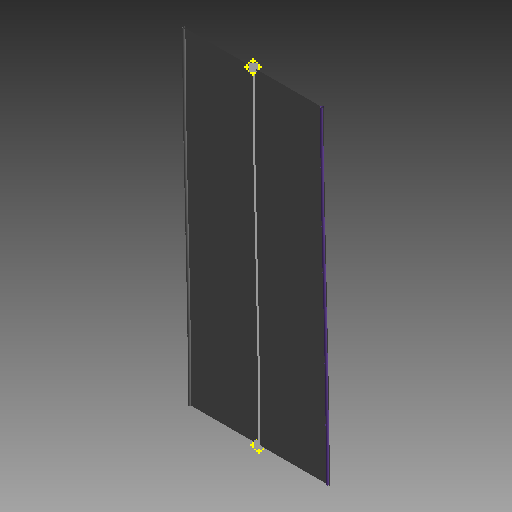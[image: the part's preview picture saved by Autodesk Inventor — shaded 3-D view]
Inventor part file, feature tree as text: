
AUTODESK INVENTOR PART (.ipt)
format: ipt  version: 2019 (Build 230136000, 136)  size: 113,664 bytes
history: native  units: mm (DEFAULTED — no unit token found)
features: other x6, sketch x3, sweep x3
ambient origin geometry x8: Origin, YZ Plane, XZ Plane, XY Plane, X Axis, Y Axis, Z Axis, Center Point
bodies: Body1 (feature_tree), Body2 (feature_tree), Body3 (feature_tree)
feature tree (12):
  other  "Work Point1"
  other  "Work Point2"
  other  "RibbonCable1"
  sketch  "Sketch1"  dims[d0=0.0mm d1=0.0mm d2=0.0mm d3=0.0mm]
  sketch  "Sketch2"  dims[d4=0.0mm d5=0.0mm]
  sketch  "Sketch3"
  other  "Srf1"
  other  "Srf2"
  other  "Srf3"
  sweep  "SweepSrf1"
  sweep  "SweepSrf2"
  sweep  "SweepSrf3"
